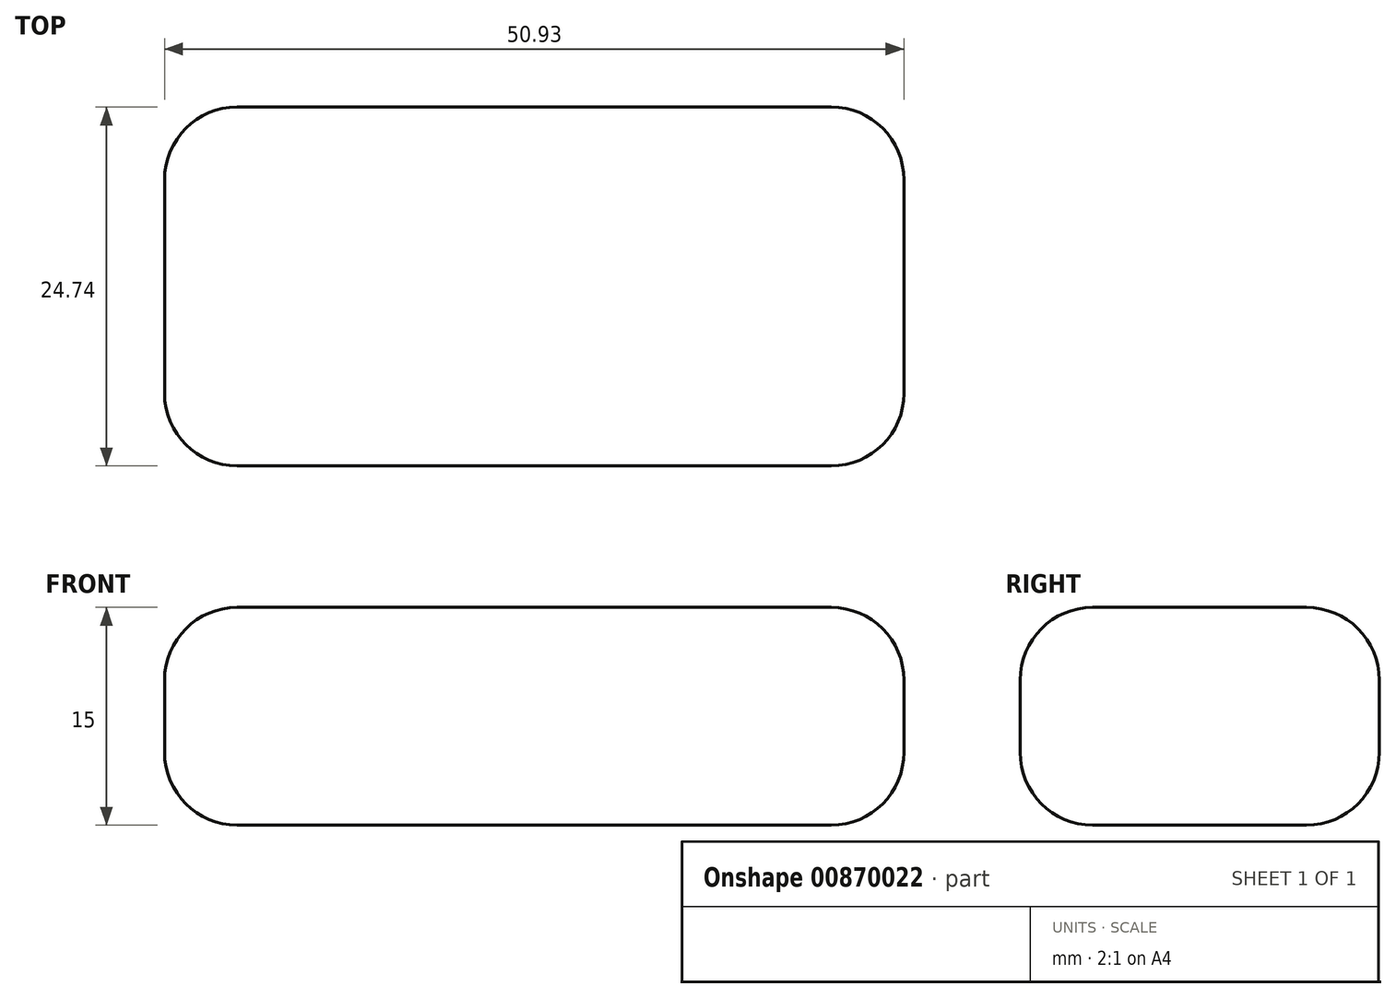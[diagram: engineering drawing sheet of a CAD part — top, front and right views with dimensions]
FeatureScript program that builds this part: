
annotation { "Feature Type Name" : "Feature", "Feature Type Description" : "" }
export const myFeature = defineFeature(function(context is Context, id is Id, definition is map)
    precondition{}
    {
        {
            var Q0;
            Q0=qCreatedBy(makeId("Top.planeOp"),FACE);
            var sketch = newSketch(context, id + "F0", { "sketchPlane" : qUnion([Q0])});
            skLineSegment(sketch, "E0.bottom", {"start": v(0, 0) * mm, "end": v(-50.93, 0) * mm});
            skLineSegment(sketch, "E0.top", {"start": v(0, -24.74) * mm, "end": v(-50.93, -24.74) * mm});
            skLineSegment(sketch, "E0.left", {"start": v(0, 0) * mm, "end": v(0, -24.74) * mm});
            skLineSegment(sketch, "E0.right", {"start": v(-50.93, 0) * mm, "end": v(-50.93, -24.74) * mm});
            skSolve(sketch);
        }
        {
            var Q0;
            Q0=makeQuery(id+"F0.imprint","IMPRINT",FACE,{"disambiguationData":[TD([[makeQuery(id+"F0.imprint","IMPRINT",EDGE,{"derivedFrom":sQuery(id+"F0.wireOp",EDGE,"E0.bottom")}),1.0]])]});
            extrude(context, id + "F1", {"entities" : qUnion([Q0]), "depth" : 15 * mm, "offsetDistance" : 25 * mm});
        }
        {
            var Q0;
            Q0=makeQuery(id+"F1.opExtrude","SWEPT_EDGE",EDGE,{"disambiguationData":[OSD([sQuery(id+"F0.wireOp",EDGE,"E0.top"),sQuery(id+"F0.wireOp",EDGE,"E0.left")])]});
            var Q1;
            Q1=makeQuery(id+"F1.opExtrude","SWEPT_EDGE",EDGE,{"disambiguationData":[OSD([sQuery(id+"F0.wireOp",EDGE,"E0.bottom"),sQuery(id+"F0.wireOp",EDGE,"E0.left")])]});
            var Q2;
            Q2=makeQuery(id+"F1.opExtrude","SWEPT_EDGE",EDGE,{"disambiguationData":[OSD([sQuery(id+"F0.wireOp",EDGE,"E0.top"),sQuery(id+"F0.wireOp",EDGE,"E0.right")])]});
            var Q3;
            Q3=makeQuery(id+"F1.opExtrude","SWEPT_EDGE",EDGE,{"disambiguationData":[OSD([sQuery(id+"F0.wireOp",EDGE,"E0.bottom"),sQuery(id+"F0.wireOp",EDGE,"E0.right")])]});
            var Q4;
            Q4=makeQuery(id+"F1.opExtrude","CAP_EDGE",EDGE,{"disambiguationData":[OSD([sQuery(id+"F0.wireOp",EDGE,"E0.bottom")])],"isStart":false});
            var Q5;
            Q5=makeQuery(id+"F1.opExtrude","CAP_EDGE",EDGE,{"disambiguationData":[OSD([sQuery(id+"F0.wireOp",EDGE,"E0.left")])],"isStart":false});
            var Q6;
            Q6=makeQuery(id+"F1.opExtrude","CAP_EDGE",EDGE,{"disambiguationData":[OSD([sQuery(id+"F0.wireOp",EDGE,"E0.top")])],"isStart":false});
            var Q7;
            Q7=makeQuery(id+"F1.opExtrude","CAP_EDGE",EDGE,{"disambiguationData":[OSD([sQuery(id+"F0.wireOp",EDGE,"E0.bottom")])],"isStart":true});
            var Q8;
            Q8=makeQuery(id+"F1.opExtrude","CAP_EDGE",EDGE,{"disambiguationData":[OSD([sQuery(id+"F0.wireOp",EDGE,"E0.left")])],"isStart":true});
            var Q9;
            Q9=makeQuery(id+"F1.opExtrude","CAP_EDGE",EDGE,{"disambiguationData":[OSD([sQuery(id+"F0.wireOp",EDGE,"E0.top")])],"isStart":true});
            var Q10;
            Q10=makeQuery(id+"F1.opExtrude","CAP_EDGE",EDGE,{"disambiguationData":[OSD([sQuery(id+"F0.wireOp",EDGE,"E0.right")])],"isStart":true});
            var Q11;
            Q11=makeQuery(id+"F1.opExtrude","CAP_EDGE",EDGE,{"disambiguationData":[OSD([sQuery(id+"F0.wireOp",EDGE,"E0.right")])],"isStart":false});
            fillet(context, id + "F2", {"entities" : qUnion([Q0, Q1, Q2, Q3, Q4, Q5, Q6, Q7, Q8, Q9, Q10, Q11]), "tangentPropagation" : true, "radius" : 5 * mm, "defaultsChanged" : false, "vertexSettings" : [], "allowEdgeOverflow" : false});
        }
    });
